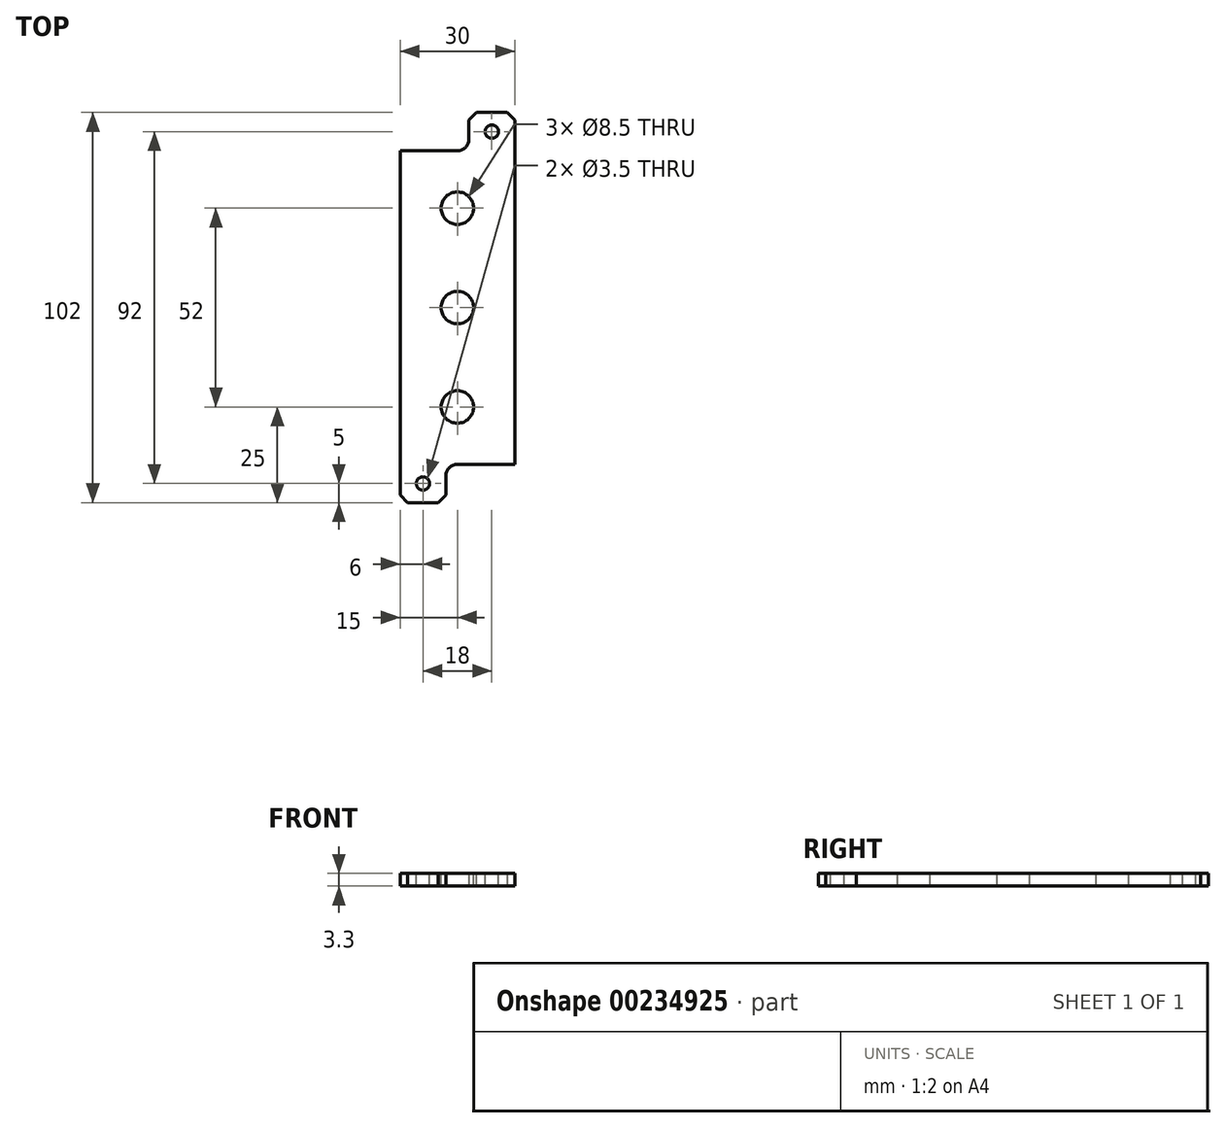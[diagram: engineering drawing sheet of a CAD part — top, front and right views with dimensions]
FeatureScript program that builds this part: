
annotation { "Feature Type Name" : "Feature", "Feature Type Description" : "" }
export const myFeature = defineFeature(function(context is Context, id is Id, definition is map)
    precondition{}
    {
        {
            var Q0;
            Q0=qCreatedBy(makeId("Top.planeOp"),FACE);
            var sketch = newSketch(context, id + "F0", { "sketchPlane" : qUnion([Q0])});
            skLineSegment(sketch, "E0.bottom", {"start": v(15, 41) * mm, "end": v(-15, 41) * mm});
            skLineSegment(sketch, "E0.top", {"start": v(15, -41) * mm, "end": v(-15, -41) * mm});
            skLineSegment(sketch, "E0.left", {"start": v(15, 41) * mm, "end": v(15, -41) * mm});
            skLineSegment(sketch, "E0.right", {"start": v(-15, 41) * mm, "end": v(-15, -41) * mm});
            skPoint(sketch, "E0.middle", {"position": v(0, 0) * mm});
            skLineSegment(sketch, "E1.bottom", {"start": v(15, 41) * mm, "end": v(3, 41) * mm});
            skLineSegment(sketch, "E1.top", {"start": v(15, 51) * mm, "end": v(3, 51) * mm});
            skLineSegment(sketch, "E1.left", {"start": v(15, 41) * mm, "end": v(15, 51) * mm});
            skLineSegment(sketch, "E1.right", {"start": v(3, 41) * mm, "end": v(3, 51) * mm});
            skLineSegment(sketch, "E2.bottom", {"start": v(-15, -41) * mm, "end": v(-3, -41) * mm});
            skLineSegment(sketch, "E2.top", {"start": v(-15, -51) * mm, "end": v(-3, -51) * mm});
            skLineSegment(sketch, "E2.left", {"start": v(-15, -41) * mm, "end": v(-15, -51) * mm});
            skLineSegment(sketch, "E2.right", {"start": v(-3, -41) * mm, "end": v(-3, -51) * mm});
            skSolve(sketch);
        }
        {
            var Q0;
            Q0=qSketchRegion(id+"F0",true);
            extrude(context, id + "F1", {"entities" : qUnion([Q0]), "depth" : 3.3 * mm});
        }
        {
            var Q0;
            Q0=makeQuery(id+"F1.opExtrude","SWEPT_EDGE",EDGE,{"disambiguationData":[OSD([sQuery(id+"F0.wireOp",EDGE,"E1.top"),sQuery(id+"F0.wireOp",EDGE,"E1.left")])]});
            var Q1;
            Q1=makeQuery(id+"F1.opExtrude","SWEPT_EDGE",EDGE,{"disambiguationData":[OSD([sQuery(id+"F0.wireOp",EDGE,"E1.top"),sQuery(id+"F0.wireOp",EDGE,"E1.right")])]});
            var Q2;
            Q2=makeQuery(id+"F1.opExtrude","SWEPT_EDGE",EDGE,{"disambiguationData":[OSD([sQuery(id+"F0.wireOp",EDGE,"E2.top"),sQuery(id+"F0.wireOp",EDGE,"E2.left")])]});
            var Q3;
            Q3=makeQuery(id+"F1.opExtrude","SWEPT_EDGE",EDGE,{"disambiguationData":[OSD([sQuery(id+"F0.wireOp",EDGE,"E2.top"),sQuery(id+"F0.wireOp",EDGE,"E2.right")])]});
            chamfer(context, id + "F2", {"entities" : qUnion([Q0, Q1, Q2, Q3]), "width" : 2 * mm, "tangentPropagation" : true});
        }
        {
            var Q0;
            Q0=makeQuery(id+"F1.opExtrude","SWEPT_EDGE",EDGE,{"disambiguationData":[OSD([sQuery(id+"F0.wireOp",EDGE,"E0.bottom"),sQuery(id+"F0.wireOp",EDGE,"E1.bottom"),sQuery(id+"F0.wireOp",EDGE,"E1.right")])]});
            fillet(context, id + "F3", {"entities" : qUnion([Q0]), "radius" : 3 * mm, "tangentPropagation" : true, "allowEdgeOverflow" : false});
        }
        {
            var Q0;
            Q0=makeQuery(id+"F1.opExtrude","SWEPT_EDGE",EDGE,{"disambiguationData":[OSD([sQuery(id+"F0.wireOp",EDGE,"E0.top"),sQuery(id+"F0.wireOp",EDGE,"E2.bottom"),sQuery(id+"F0.wireOp",EDGE,"E2.right")])]});
            fillet(context, id + "F4", {"entities" : qUnion([Q0]), "radius" : 3 * mm, "tangentPropagation" : true, "allowEdgeOverflow" : false});
        }
        {
            var Q0;
            Q0=makeQuery(id+"F1.opExtrude","CAP_FACE",FACE,{"disambiguationData":[OSD([sQuery(id+"F0.wireOp",EDGE,"E0.bottom"),sQuery(id+"F0.wireOp",EDGE,"E0.top"),sQuery(id+"F0.wireOp",EDGE,"E0.left"),sQuery(id+"F0.wireOp",EDGE,"E0.right"),sQuery(id+"F0.wireOp",EDGE,"E1.top"),sQuery(id+"F0.wireOp",EDGE,"E1.left"),sQuery(id+"F0.wireOp",EDGE,"E1.right"),sQuery(id+"F0.wireOp",EDGE,"E2.top"),sQuery(id+"F0.wireOp",EDGE,"E2.left"),sQuery(id+"F0.wireOp",EDGE,"E2.right")])],"isStart":false});
            var sketch = newSketch(context, id + "F5", { "sketchPlane" : qUnion([Q0])});
            skLineSegment(sketch, "E3", {"start": v(9, 51) * mm, "end": v(9, 41) * mm, "construction": true});
            skCircle(sketch, "E4", {"center": v(9, 46) * mm, "radius": 1.75 * mm});
            skLineSegment(sketch, "E5", {"start": v(-9, -51) * mm, "end": v(-9, -41) * mm, "construction": true});
            skCircle(sketch, "E6", {"center": v(-9, -46) * mm, "radius": 1.75 * mm});
            skSolve(sketch);
        }
        {
            var Q0;
            Q0=qSketchRegion(id+"F5",true);
            extrude(context, id + "F6", {"entities" : qUnion([Q0]), "operationType" : NewBodyOperationType.REMOVE, "oppositeDirection" : true, "depth" : 25 * mm});
        }
        {
            var Q0;
            Q0=makeQuery(id+"F1.opExtrude","CAP_FACE",FACE,{"disambiguationData":[OSD([sQuery(id+"F0.wireOp",EDGE,"E0.bottom"),sQuery(id+"F0.wireOp",EDGE,"E0.top"),sQuery(id+"F0.wireOp",EDGE,"E0.left"),sQuery(id+"F0.wireOp",EDGE,"E0.right"),sQuery(id+"F0.wireOp",EDGE,"E1.top"),sQuery(id+"F0.wireOp",EDGE,"E1.left"),sQuery(id+"F0.wireOp",EDGE,"E1.right"),sQuery(id+"F0.wireOp",EDGE,"E2.top"),sQuery(id+"F0.wireOp",EDGE,"E2.left"),sQuery(id+"F0.wireOp",EDGE,"E2.right")])],"isStart":false});
            var sketch = newSketch(context, id + "F7", { "sketchPlane" : qUnion([Q0])});
            skLineSegment(sketch, "E7", {"start": v(0, 41) * mm, "end": v(0, 0) * mm, "construction": true});
            skLineSegment(sketch, "E8", {"start": v(0, 0) * mm, "end": v(0, -41) * mm, "construction": true});
            skCircle(sketch, "E9", {"center": v(0, 26) * mm, "radius": 2.5 * mm});
            skCircle(sketch, "E10", {"center": v(0, -26) * mm, "radius": 2.5 * mm});
            skSolve(sketch);
        }
        {
            var Q0;
            Q0=qSketchRegion(id+"F7",true);
            extrude(context, id + "F8", {"entities" : qUnion([Q0]), "operationType" : NewBodyOperationType.REMOVE, "oppositeDirection" : true, "depth" : 25 * mm});
        }
        {
            var Q0;
            Q0=makeQuery(id+"F1.opExtrude","CAP_FACE",FACE,{"disambiguationData":[OSD([sQuery(id+"F0.wireOp",EDGE,"E0.bottom"),sQuery(id+"F0.wireOp",EDGE,"E0.top"),sQuery(id+"F0.wireOp",EDGE,"E0.left"),sQuery(id+"F0.wireOp",EDGE,"E0.right"),sQuery(id+"F0.wireOp",EDGE,"E1.top"),sQuery(id+"F0.wireOp",EDGE,"E1.left"),sQuery(id+"F0.wireOp",EDGE,"E1.right"),sQuery(id+"F0.wireOp",EDGE,"E2.top"),sQuery(id+"F0.wireOp",EDGE,"E2.left"),sQuery(id+"F0.wireOp",EDGE,"E2.right")])],"isStart":false});
            var sketch = newSketch(context, id + "F9", { "sketchPlane" : qUnion([Q0])});
            skCircle(sketch, "E11", {"center": v(0, 26) * mm, "radius": 4.25 * mm});
            skCircle(sketch, "E12", {"center": v(0, -26) * mm, "radius": 4.25 * mm});
            skCircle(sketch, "E13", {"center": v(0, 0) * mm, "radius": 4.25 * mm});
            skSolve(sketch);
        }
        {
            var Q0;
            Q0 = qSketchRegion(id + "F9", true);
            extrude(context, id + "F10", {"entities" : qUnion([Q0]), "operationType" : NewBodyOperationType.REMOVE, "oppositeDirection" : true, "depth" : 25 * mm, "offsetDistance" : 25 * mm});
        }
    });
